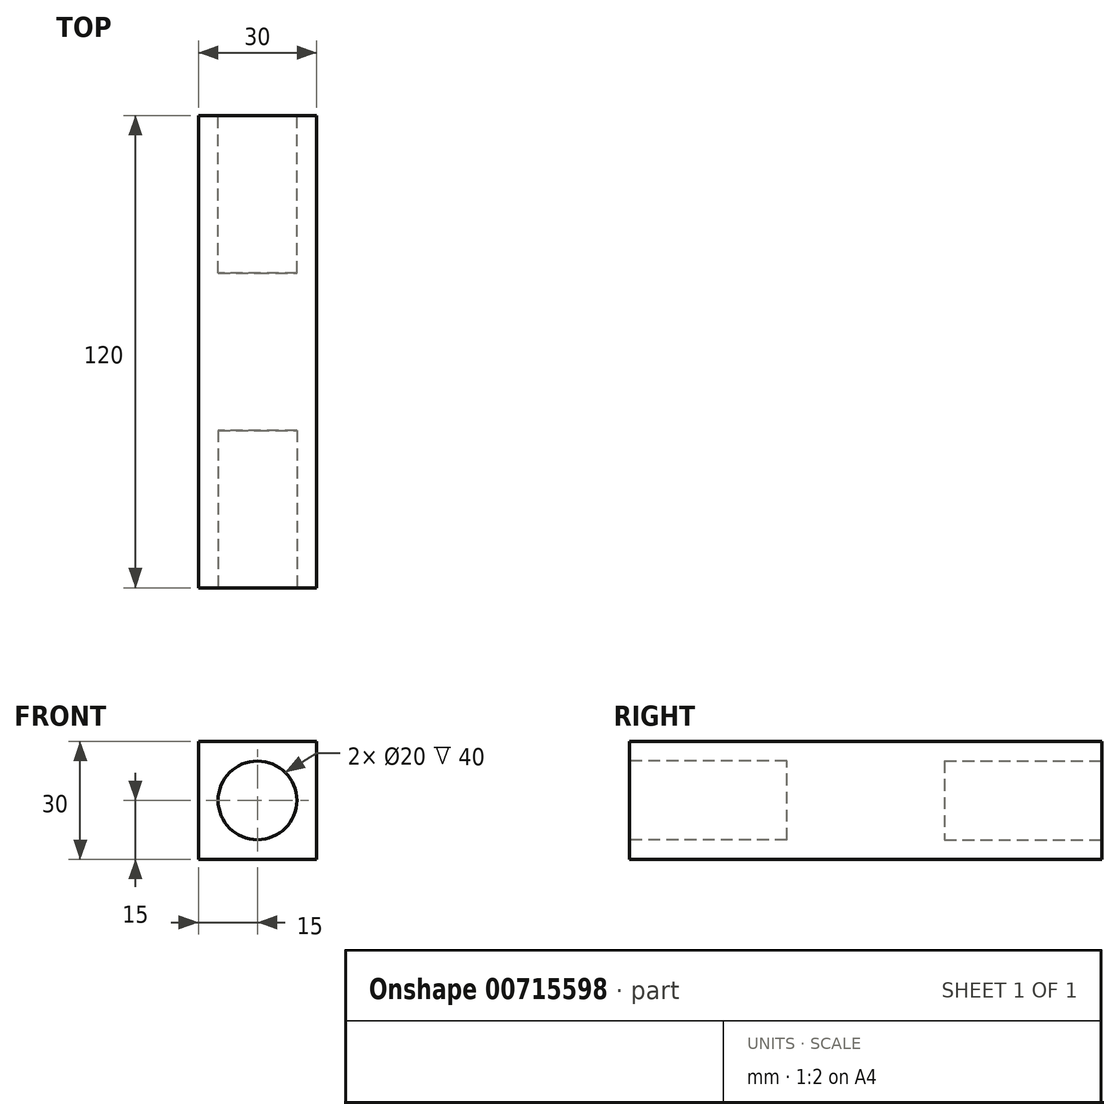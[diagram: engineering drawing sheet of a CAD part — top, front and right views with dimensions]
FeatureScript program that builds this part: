
annotation { "Feature Type Name" : "Feature", "Feature Type Description" : "" }
export const myFeature = defineFeature(function(context is Context, id is Id, definition is map)
    precondition{}
    {
        {
            var Q0;
            Q0=qCreatedBy(makeId("Front.planeOp"),FACE);
            var sketch = newSketch(context, id + "F0", { "sketchPlane" : qUnion([Q0])});
            skLineSegment(sketch, "E0.bottom", {"start": v(15, -15) * mm, "end": v(-15, -15) * mm});
            skLineSegment(sketch, "E0.top", {"start": v(15, 15) * mm, "end": v(-15, 15) * mm});
            skLineSegment(sketch, "E0.left", {"start": v(15, -15) * mm, "end": v(15, 15) * mm});
            skLineSegment(sketch, "E0.right", {"start": v(-15, -15) * mm, "end": v(-15, 15) * mm});
            skPoint(sketch, "E0.middle", {"position": v(0, 0) * mm});
            skSolve(sketch);
        }
        {
            var Q0;
            Q0 = qSketchRegion(id + "F0", true);
            extrude(context, id + "F1", {"entities" : qUnion([Q0]), "endBound" : BoundingType.SYMMETRIC, "depth" : 120 * mm, "offsetDistance" : 25 * mm});
        }
        {
            var Q0;
            Q0=makeQuery(id+"F1.opExtrude","CAP_FACE",FACE,{"disambiguationData":[OSD([sQuery(id+"F0.wireOp",EDGE,"E0.bottom"),sQuery(id+"F0.wireOp",EDGE,"E0.top"),sQuery(id+"F0.wireOp",EDGE,"E0.left"),sQuery(id+"F0.wireOp",EDGE,"E0.right")])],"isStart":false});
            var sketch = newSketch(context, id + "F2", { "sketchPlane" : qUnion([Q0])});
            skCircle(sketch, "E1", {"center": v(0, 0) * mm, "radius": 10 * mm});
            skSolve(sketch);
        }
        {
            var Q0;
            Q0 = qSketchRegion(id + "F2", true);
            extrude(context, id + "F3", {"entities" : qUnion([Q0]), "operationType" : NewBodyOperationType.REMOVE, "oppositeDirection" : true, "depth" : 40 * mm, "offsetDistance" : 25 * mm});
        }
        {
            var Q0;
            Q0=makeQuery(id+"F1.opExtrude","CAP_FACE",FACE,{"disambiguationData":[OSD([sQuery(id+"F0.wireOp",EDGE,"E0.bottom"),sQuery(id+"F0.wireOp",EDGE,"E0.top"),sQuery(id+"F0.wireOp",EDGE,"E0.left"),sQuery(id+"F0.wireOp",EDGE,"E0.right")])],"isStart":true});
            var sketch = newSketch(context, id + "F4", { "sketchPlane" : qUnion([Q0])});
            skCircle(sketch, "E2", {"center": v(0, 0) * mm, "radius": 10 * mm});
            skSolve(sketch);
        }
        {
            var Q0;
            Q0 = qSketchRegion(id + "F4", true);
            extrude(context, id + "F5", {"entities" : qUnion([Q0]), "operationType" : NewBodyOperationType.REMOVE, "oppositeDirection" : true, "depth" : 40 * mm, "offsetDistance" : 25 * mm});
        }
    });
